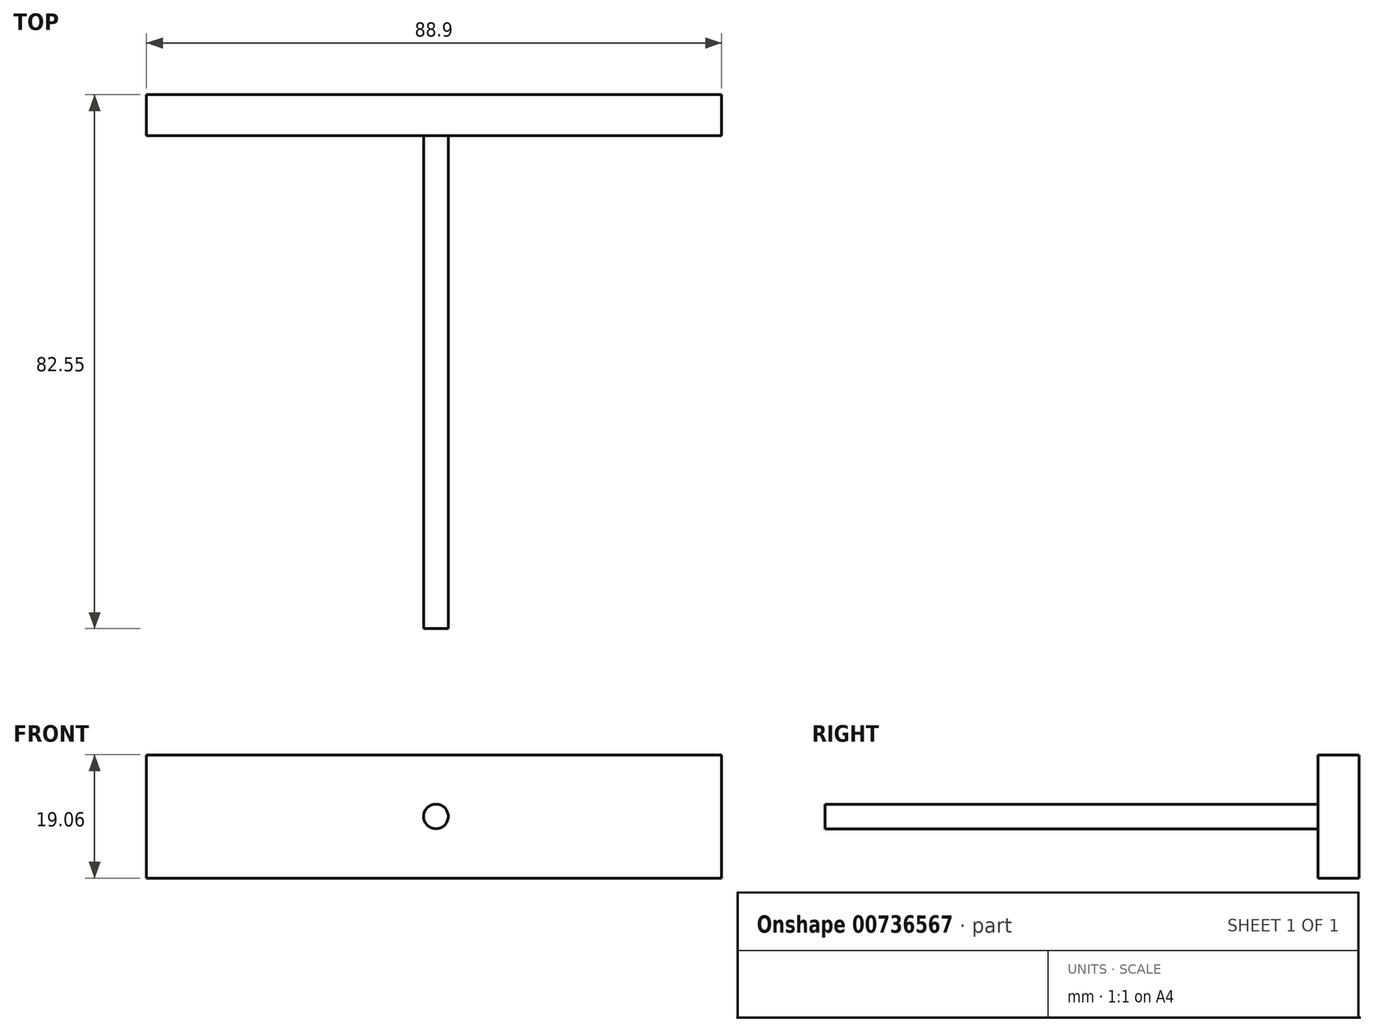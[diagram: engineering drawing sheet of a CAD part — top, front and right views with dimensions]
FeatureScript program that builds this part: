
annotation { "Feature Type Name" : "Feature", "Feature Type Description" : "" }
export const myFeature = defineFeature(function(context is Context, id is Id, definition is map)
    precondition{}
    {
        {
            var Q0;
            Q0=qCreatedBy(makeId("Front.planeOp"),FACE);
            var sketch = newSketch(context, id + "F0", { "sketchPlane" : qUnion([Q0])});
            skCircle(sketch, "E0", {"center": v(0, 0) * mm, "radius": 1.9 * mm});
            skSolve(sketch);
        }
        {
            var Q0;
            Q0 = qSketchRegion(id + "F0", true);
            extrude(context, id + "F1", {"entities" : qUnion([Q0]), "depth" : 76.2 * mm, "offsetDistance" : 25.4 * mm});
        }
        {
            var Q0;
            Q0=qCreatedBy(makeId("Front.planeOp"),FACE);
            var sketch = newSketch(context, id + "F2", { "sketchPlane" : qUnion([Q0])});
            skLineSegment(sketch, "E1.bottom", {"start": v(-44.74, 9.53) * mm, "end": v(44.16, 9.53) * mm});
            skLineSegment(sketch, "E1.top", {"start": v(-44.74, -9.53) * mm, "end": v(44.16, -9.53) * mm});
            skLineSegment(sketch, "E1.left", {"start": v(-44.74, 9.53) * mm, "end": v(-44.74, -9.53) * mm});
            skLineSegment(sketch, "E1.right", {"start": v(44.16, 9.53) * mm, "end": v(44.16, -9.53) * mm});
            skSolve(sketch);
        }
        {
            var Q0;
            Q0 = qSketchRegion(id + "F2", true);
            extrude(context, id + "F3", {"entities" : qUnion([Q0]), "operationType" : NewBodyOperationType.ADD, "oppositeDirection" : true, "depth" : 6.35 * mm, "offsetDistance" : 25.4 * mm});
        }
    });
